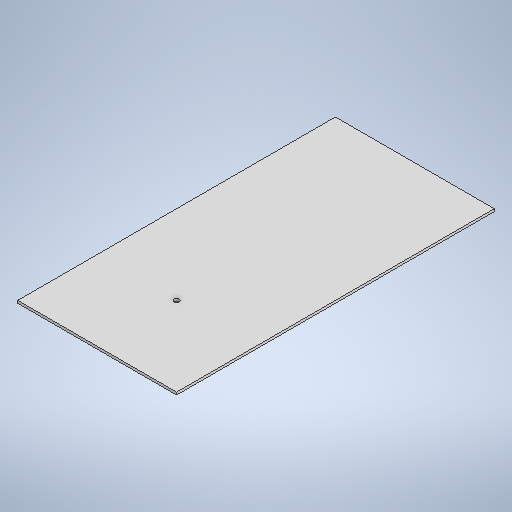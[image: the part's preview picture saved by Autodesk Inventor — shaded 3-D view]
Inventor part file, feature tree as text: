
AUTODESK INVENTOR PART (.ipt)
format: ipt  version: 2025.2 (Build 292293000, 293)  size: 225,280 bytes
history: native  units: mm
features: extrude x2, sketch x2
ambient origin geometry x8: Origin, YZ Plane, XZ Plane, XY Plane, X Axis, Y Axis, Z Axis, Center Point
bodies: Solid1 (feature_tree)
feature tree (4):
  extrude  "Extrusion1"  Depth=300.0mm
  extrude  "Extrusion2"  Depth=3.175mm TaperAngle=0.0deg
  sketch  "Sketch1"  dims[d0=200.0mm d1=300.0mm]
  sketch  "Sketch2"  dims[d2=100.0mm d3=3.175mm d4=0.0mm d6=6.35mm d7=3.175mm d8=0.0mm]
